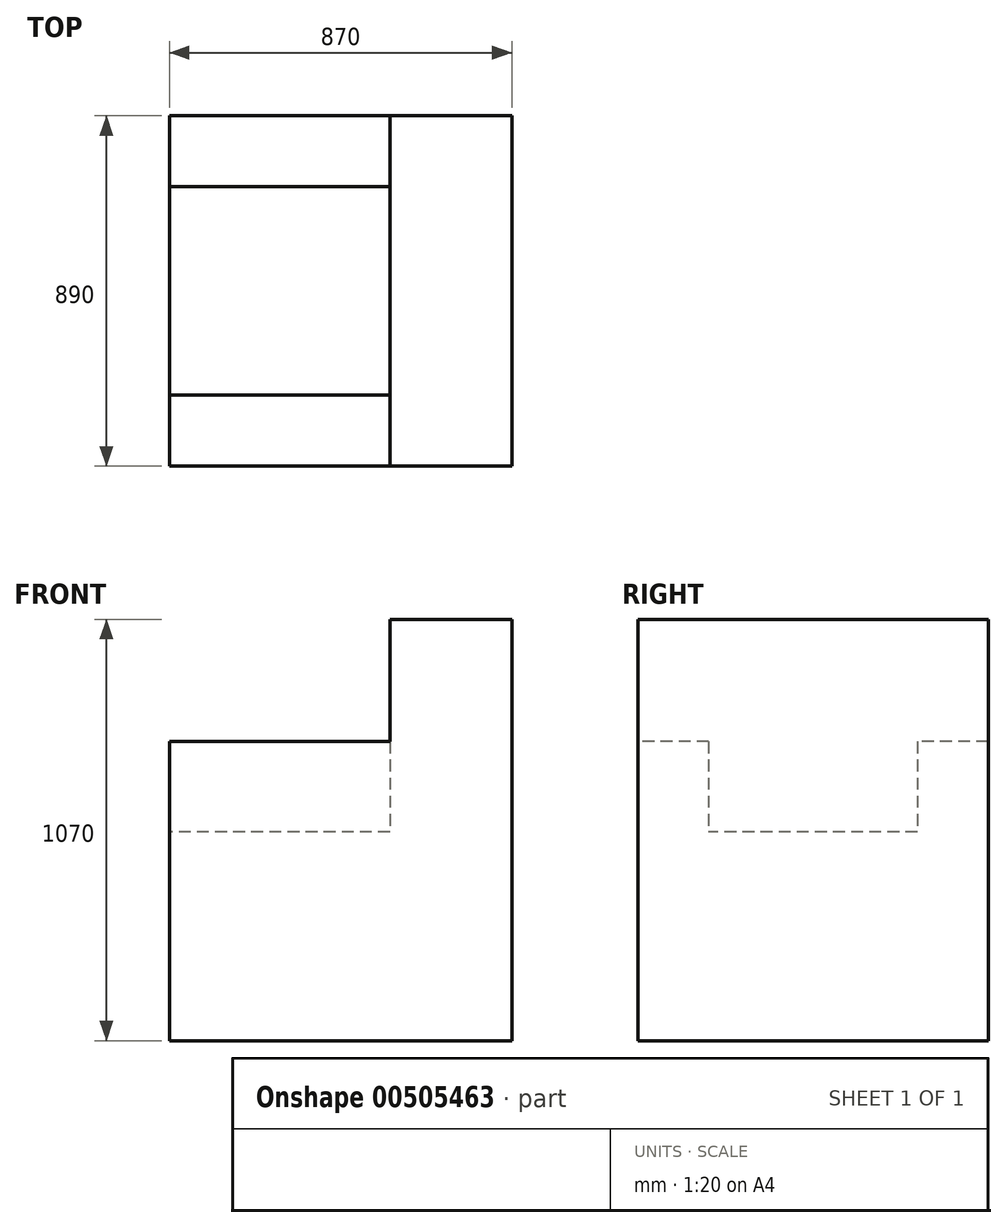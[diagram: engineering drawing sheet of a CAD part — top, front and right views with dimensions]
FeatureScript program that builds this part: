
annotation { "Feature Type Name" : "Feature", "Feature Type Description" : "" }
export const myFeature = defineFeature(function(context is Context, id is Id, definition is map)
    precondition{}
    {
        {
            var Q0;
            Q0=qCreatedBy(makeId("Top.planeOp"),FACE);
            var sketch = newSketch(context, id + "F0", { "sketchPlane" : qUnion([Q0])});
            skLineSegment(sketch, "E0.bottom", {"start": v(-435, 445) * mm, "end": v(435, 445) * mm});
            skLineSegment(sketch, "E0.top", {"start": v(-435, -445) * mm, "end": v(435, -445) * mm});
            skLineSegment(sketch, "E0.left", {"start": v(-435, 445) * mm, "end": v(-435, -445) * mm});
            skLineSegment(sketch, "E0.right", {"start": v(435, 445) * mm, "end": v(435, -445) * mm});
            skPoint(sketch, "E0.middle", {"position": v(0, 0) * mm});
            skSolve(sketch);
        }
        {
            var Q0;
            Q0 = qSketchRegion(id + "F0", true);
            extrude(context, id + "F1", {"entities" : qUnion([Q0]), "depth" : 1070 * mm});
        }
        {
            var Q0;
            Q0=makeQuery(id+"F1.opExtrude","SWEPT_FACE",FACE,{"disambiguationData":[OSD([sQuery(id+"F0.wireOp",EDGE,"E0.left")])]});
            var sketch = newSketch(context, id + "F2", { "sketchPlane" : qUnion([Q0])});
            skLineSegment(sketch, "E1.bottom", {"start": v(-265, 1070) * mm, "end": v(265, 1070) * mm});
            skLineSegment(sketch, "E1.top", {"start": v(-265, 530) * mm, "end": v(265, 530) * mm});
            skLineSegment(sketch, "E1.left", {"start": v(265, 1070) * mm, "end": v(265, 530) * mm});
            skLineSegment(sketch, "E1.right", {"start": v(-265, 1070) * mm, "end": v(-265, 530) * mm});
            skLineSegment(sketch, "E2", {"start": v(0, 1070) * mm, "end": v(0, 530) * mm, "construction": true});
            skSolve(sketch);
        }
        {
            var Q0;
            Q0 = qSketchRegion(id + "F2", true);
            extrude(context, id + "F3", {"entities" : qUnion([Q0]), "operationType" : NewBodyOperationType.REMOVE, "oppositeDirection" : true, "depth" : 560 * mm});
        }
        {
            var Q0;
            Q0=makeQuery(id+"F1.opExtrude","SWEPT_FACE",FACE,{"disambiguationData":[OSD([sQuery(id+"F0.wireOp",EDGE,"E0.left")])]});
            var sketch = newSketch(context, id + "F4", { "sketchPlane" : qUnion([Q0])});
            skLineSegment(sketch, "E3.bottom", {"start": v(-445, 1070) * mm, "end": v(-265, 1070) * mm});
            skLineSegment(sketch, "E3.top", {"start": v(-445, 760) * mm, "end": v(-265, 760) * mm});
            skLineSegment(sketch, "E3.left", {"start": v(-445, 1070) * mm, "end": v(-445, 760) * mm});
            skLineSegment(sketch, "E3.right", {"start": v(-265, 1070) * mm, "end": v(-265, 760) * mm});
            skLineSegment(sketch, "E4.bottom", {"start": v(265, 1070) * mm, "end": v(445, 1070) * mm});
            skLineSegment(sketch, "E4.top", {"start": v(265, 760) * mm, "end": v(445, 760) * mm});
            skLineSegment(sketch, "E4.left", {"start": v(265, 1070) * mm, "end": v(265, 760) * mm});
            skLineSegment(sketch, "E4.right", {"start": v(445, 1070) * mm, "end": v(445, 760) * mm});
            skSolve(sketch);
        }
        {
            var Q0;
            Q0 = qSketchRegion(id + "F4", true);
            var Q1;
            Q1=makeQuery(id+"F3.boolean.opBoolean","COPY",FACE,{"derivedFrom":makeQuery(id+"F3.opExtrude","CAP_FACE",FACE,{"disambiguationData":[OSD([sQuery(id+"F2.wireOp",EDGE,"E1.bottom"),sQuery(id+"F2.wireOp",EDGE,"E1.top"),sQuery(id+"F2.wireOp",EDGE,"E1.left"),sQuery(id+"F2.wireOp",EDGE,"E1.right")])],"isStart":false})});
            extrude(context, id + "F5", {"entities" : qUnion([Q0]), "operationType" : NewBodyOperationType.REMOVE, "endBound" : BoundingType.UP_TO_SURFACE, "oppositeDirection" : true, "endBoundEntityFace" : qUnion([Q1]), "depth" : 25 * mm});
        }
    });
